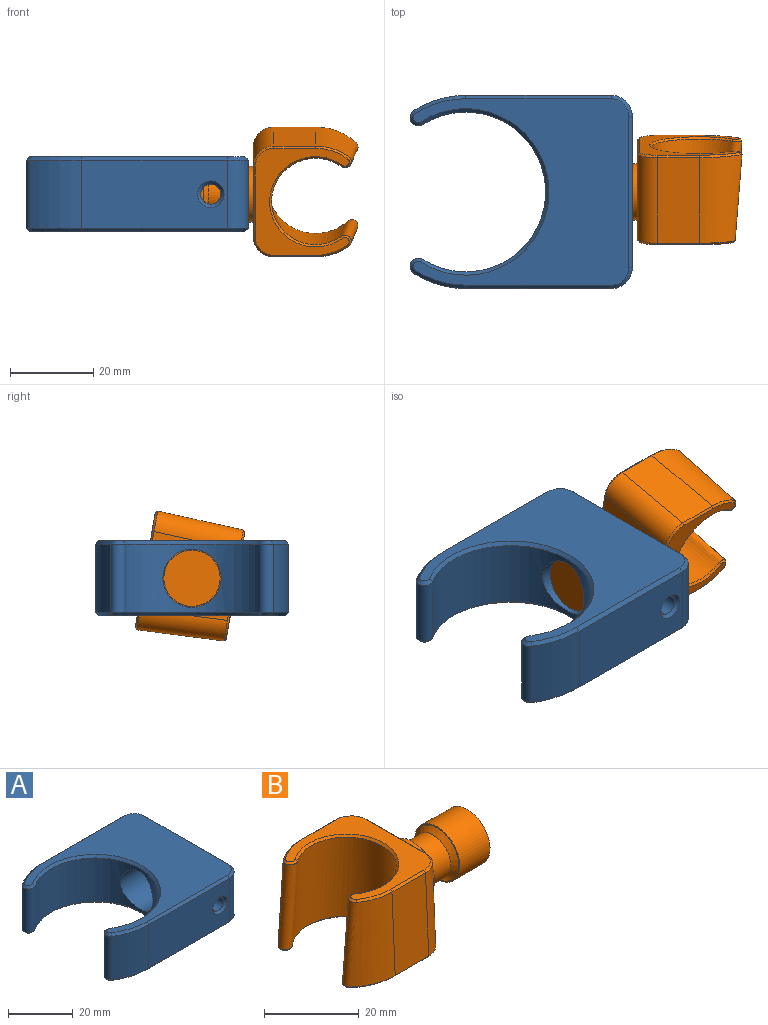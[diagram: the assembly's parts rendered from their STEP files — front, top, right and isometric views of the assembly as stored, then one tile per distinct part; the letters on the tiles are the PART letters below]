
ASSEMBLY  parts=2 mates=1
PART A: 35 faces, bbox 53.4x46.4x18 mm
  f0: cylinder r=23.2mm len=16.4mm, axis (0,0,-1), area 215.8mm2, adj f1,f7,f20,f27
  f1: cylinder r=2mm len=16.4mm, axis (0,0,-1), area 103mm2, adj f0,f2,f22,f25
  f2: cylinder r=19.2mm len=38.4mm, axis (0,0,-1), area 1190mm2, adj f1,f3,f10,f23,f24
  f3: cylinder r=2mm len=16.4mm, axis (0,0,-1), area 103mm2, adj f2,f4,f21,f26
  f4: cylinder r=23.2mm len=16.4mm, axis (0,0,-1), area 215.8mm2, adj f3,f5,f19,f28
  f5: plane 35x16.4mm, normal (0,-1,0), area 541.8mm2, adj f4,f12,f17,f30,f34
  f6: plane 36.4x16.4mm, normal (1,0,0), area 443mm2, adj f10,f12,f13,f14,f33
  f7: plane 35x16.4mm, normal (0,1,0), area 574mm2, adj f0,f13,f18,f29
  f8: plane 51.79x44.8mm, normal (0,0,1), area 1182.5mm2, adj f24,f25,f26,f27,f28,f29,f30,f31
  f9: plane 51.79x44.8mm, normal (0,0,-1), area 1182.5mm2, adj f14,f15,f16,f17,f18,f19,f20,f21
  f10: cylinder r=7mm len=22.12mm, axis (1,0,0), area 925.4mm2, adj f2,f6,f11
  f11: cylinder r=2.4mm len=15.82mm, axis (0,-1,0), area 235.4mm2, adj f10,f34
  f12: cylinder r=5mm len=16.4mm, axis (0,0,-1), area 128.8mm2, adj f5,f6,f15,f32
  f13: cylinder r=5mm len=16.4mm, axis (0,0,-1), area 128.8mm2, adj f6,f7,f16,f31
  f14: plane 36.4x0.8mm, normal (0.71,0,-0.71), area 41.2mm2, adj f6,f9,f15,f16
  f15: cone r=4.2mm half-angle=45deg, axis (0,0,1), area 8.2mm2, adj f9,f12,f14,f17
  f16: cone r=4.2mm half-angle=45deg, axis (0,0,1), area 8.2mm2, adj f9,f13,f14,f18
  f17: plane 35x0.8mm, normal (0,-0.71,-0.71), area 39.6mm2, adj f5,f9,f15,f19
  f18: plane 35x0.8mm, normal (0,0.71,-0.71), area 39.6mm2, adj f7,f9,f16,f20
  f19: cone r=22.4mm half-angle=45deg, axis (0,0,1), area 14.6mm2, adj f4,f9,f17,f21
  f20: cone r=22.4mm half-angle=45deg, axis (0,0,1), area 14.6mm2, adj f0,f9,f18,f22
  f21: cone r=2mm half-angle=45deg, axis (0,0,1), area 5.7mm2, adj f3,f9,f19,f23
  f22: cone r=2mm half-angle=45deg, axis (0,0,1), area 5.7mm2, adj f1,f9,f20,f23
  f23: cone r=20mm half-angle=45deg, axis (0,0,-1), area 94.8mm2, adj f2,f9,f21,f22
  f24: cone r=19.2mm half-angle=45deg, axis (0,0,1), area 94.8mm2, adj f2,f8,f25,f26
  f25: cone r=1.2mm half-angle=45deg, axis (0,0,-1), area 5.7mm2, adj f1,f8,f24,f27
  f26: cone r=1.2mm half-angle=45deg, axis (0,0,-1), area 5.7mm2, adj f3,f8,f24,f28
  f27: cone r=23.2mm half-angle=45deg, axis (0,0,-1), area 14.6mm2, adj f0,f8,f25,f29
  f28: cone r=23.2mm half-angle=45deg, axis (0,0,-1), area 14.6mm2, adj f4,f8,f26,f30
  f29: plane 35x0.8mm, normal (0,0.71,0.71), area 39.6mm2, adj f7,f8,f27,f31
  f30: plane 35x0.8mm, normal (0,-0.71,0.71), area 39.6mm2, adj f5,f8,f28,f32
  f31: cone r=4.2mm half-angle=45deg, axis (0,0,-1), area 8.2mm2, adj f8,f13,f29,f33
  f32: cone r=4.2mm half-angle=45deg, axis (0,0,-1), area 8.2mm2, adj f8,f12,f30,f33
  f33: plane 36.4x0.8mm, normal (0.71,0,0.71), area 41.2mm2, adj f6,f8,f31,f32
  f34: cone r=2.4mm half-angle=45deg, axis (0,-1,0), area 19.9mm2, adj f5,f11
PART B: 36 faces, bbox 46.3x29x22 mm
  f0: plane 28.04x24.31mm, normal (0,0,-1), area 215.6mm2, adj f26,f27,f28,f29,f30,f31,f32,f33
  f1: plane 26.12x22.66mm, normal (0,0,1), area 214.2mm2, adj f16,f17,f18,f19,f20,f21,f22,f23
  f2: plane 21.04x18.95mm, normal (1,0,0), area 235.4mm2, adj f6,f14,f15,f20,f30
  f3: plane 21.05x10mm, normal (0,1,0.05), area 210.7mm2, adj f4,f14,f16,f26
  f4: bspline ~29x25.26mm, area 1647.7mm2, adj f3,f5,f17,f19,f21,f23,f25,f27
  f5: plane 21.04x10mm, normal (0,-1,0.05), area 210.7mm2, adj f4,f15,f24,f34
  f6: cylinder r=6.75mm len=13.5mm, axis (-1,0,0), area 190.9mm2, adj f2,f7
  f7: plane 13.5x13.5mm, normal (1,0,0), area 12.4mm2, adj f6,f12
  f8: cylinder r=5.25mm len=10.5mm, axis (-1,0,0), area 168.2mm2, adj f12,f13
  f9: cylinder r=6.75mm len=13.5mm, axis (-1,0,0), area 381.7mm2, adj f10,f11
  f10: plane 13.5x13.5mm, normal (1,0,0), area 143.1mm2, adj f9
  f11: plane 13.5x13.5mm, normal (-1,0,0), area 12.4mm2, adj f9,f13
  f12: cone r=5.25mm half-angle=45deg, axis (-1,0,0), area 62.4mm2, adj f7,f8
  f13: cone r=6.45mm half-angle=45deg, axis (1,0,0), area 62.4mm2, adj f8,f11
  f14: cylinder r=5mm len=21.48mm, axis (0,-0.05,1), area 165.5mm2, adj f2,f3,f18,f28
  f15: cylinder r=5mm len=21.48mm, axis (0,0.05,1), area 165.5mm2, adj f2,f5,f22,f32
  f16: plane 10x0.48mm, normal (0,0.69,0.72), area 6.6mm2, adj f1,f3,f17,f18
  f17: bspline ~7.94x2.97mm, area 5.5mm2, adj f1,f4,f16,f19
  f18: bspline ~5.01x5.01mm, area 5mm2, adj f1,f14,f16,f20
  f19: bspline ~2.78x2.45mm, area 2.7mm2, adj f1,f4,f17,f21
  f20: plane 17.03x0.48mm, normal (0.71,0,0.71), area 11.5mm2, adj f1,f2,f18,f22
  f21: bspline ~22.09x17.46mm, area 32.7mm2, adj f1,f4,f19,f23
  f22: bspline ~5.01x5.01mm, area 5mm2, adj f1,f15,f20,f24
  f23: bspline ~2.78x2.45mm, area 2.7mm2, adj f1,f4,f21,f25
  f24: plane 10x0.48mm, normal (0,-0.69,0.72), area 6.6mm2, adj f1,f5,f22,f25
  f25: bspline ~7.94x2.97mm, area 5.5mm2, adj f1,f4,f23,f24
  f26: plane 10x0.5mm, normal (0,0.72,-0.69), area 6.9mm2, adj f0,f3,f27,f28
  f27: bspline ~9.75x4.12mm, area 7.3mm2, adj f0,f4,f26,f29
  f28: bspline ~5.01x5.01mm, area 5.1mm2, adj f0,f14,f26,f30
  f29: bspline ~2.61x2.5mm, area 2.7mm2, adj f0,f4,f27,f31
  f30: plane 18.95x0.48mm, normal (0.71,0,-0.71), area 12.8mm2, adj f0,f2,f28,f32
  f31: bspline ~24.01x20mm, area 35.7mm2, adj f0,f4,f29,f33
  f32: bspline ~5.01x5.01mm, area 5.1mm2, adj f0,f15,f30,f34
  f33: bspline ~2.61x2.5mm, area 2.7mm2, adj f0,f4,f31,f35
  f34: plane 10x0.5mm, normal (0,-0.72,-0.69), area 6.9mm2, adj f0,f5,f32,f35
  f35: bspline ~9.75x4.12mm, area 7.3mm2, adj f0,f4,f33,f34
PLACE A t=(-24.02,0,0)mm
PLACE B rot(axis=(0,-0.77,0.64),180deg) t=(32.14,11.22,10.96)mm
MATE cylindrical B.f9 <-> A.f10  axis (-1,0,0) through (-3.86,0,9)mm
